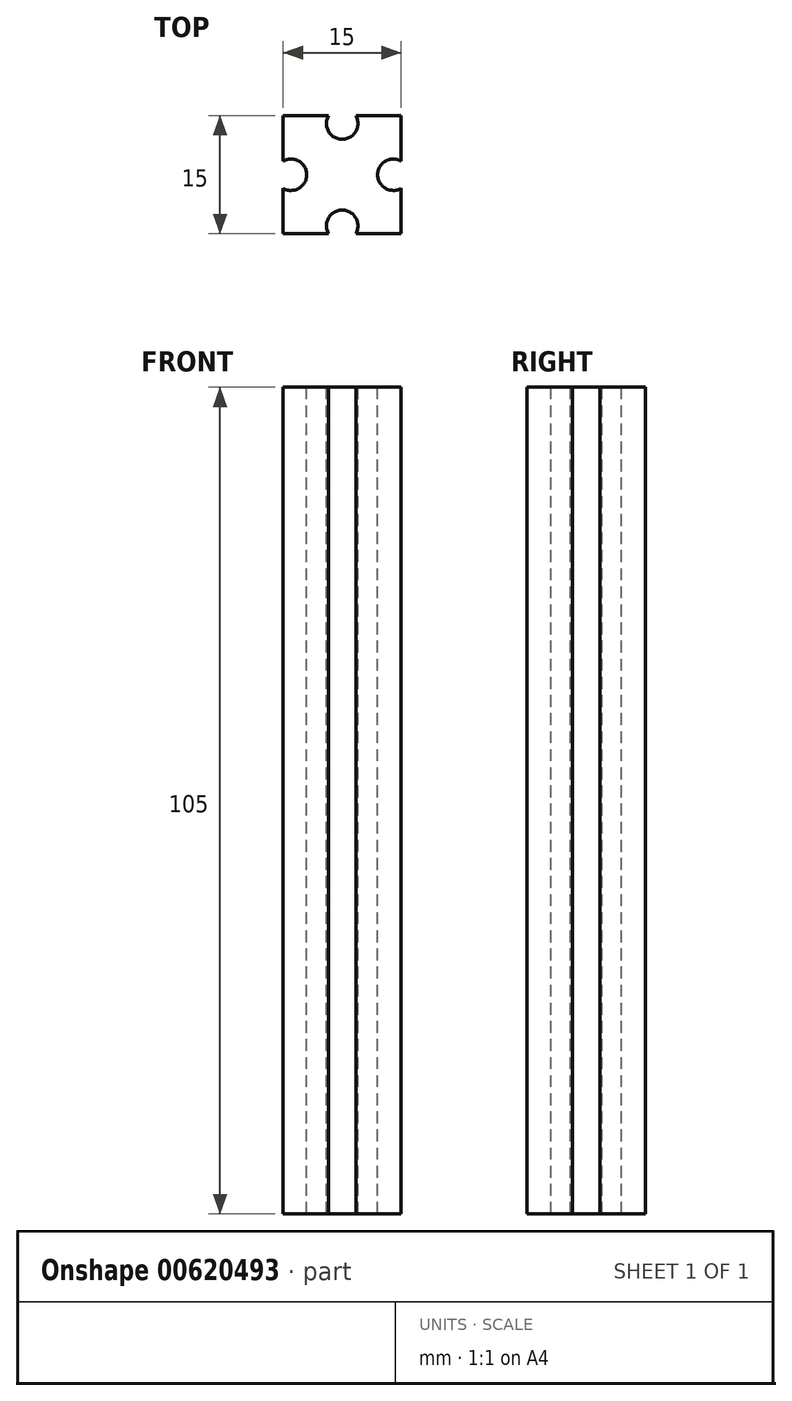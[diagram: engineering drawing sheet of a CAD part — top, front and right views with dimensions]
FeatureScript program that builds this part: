
annotation { "Feature Type Name" : "Feature", "Feature Type Description" : "" }
export const myFeature = defineFeature(function(context is Context, id is Id, definition is map)
    precondition{}
    {
        {
            var Q0;
            Q0=qCreatedBy(makeId("Top.planeOp"),FACE);
            var sketch = newSketch(context, id + "F0", { "sketchPlane" : qUnion([Q0])});
            skLineSegment(sketch, "E0.bottom", {"start": v(-11.37, 10.06) * mm, "end": v(3.63, 10.06) * mm});
            skLineSegment(sketch, "E0.top", {"start": v(-11.37, -4.94) * mm, "end": v(3.63, -4.94) * mm});
            skLineSegment(sketch, "E0.left", {"start": v(-11.37, 10.06) * mm, "end": v(-11.37, -4.94) * mm});
            skLineSegment(sketch, "E0.right", {"start": v(3.63, 10.06) * mm, "end": v(3.63, -4.94) * mm});
            skSolve(sketch);
        }
        {
            var Q0;
            Q0=makeQuery(id+"F0.imprint","IMPRINT",FACE,{"disambiguationData":[TD([[makeQuery(id+"F0.imprint","IMPRINT",EDGE,{"derivedFrom":sQuery(id+"F0.wireOp",EDGE,"E0.bottom")}),-1.0]])]});
            extrude(context, id + "F1", {"entities" : qUnion([Q0]), "depth" : 105 * mm, "offsetDistance" : 25.4 * mm});
        }
        {
            var Q0;
            Q0=makeQuery(id+"F1.opExtrude","CAP_FACE",FACE,{"disambiguationData":[OSD([sQuery(id+"F0.wireOp",EDGE,"E0.bottom"),sQuery(id+"F0.wireOp",EDGE,"E0.top"),sQuery(id+"F0.wireOp",EDGE,"E0.left"),sQuery(id+"F0.wireOp",EDGE,"E0.right")])],"isStart":false});
            var sketch = newSketch(context, id + "F2", { "sketchPlane" : qUnion([Q0])});
            skCircle(sketch, "E1", {"center": v(-10.37, 2.56) * mm, "radius": 2 * mm});
            skPoint(sketch, "E1.centerSnap0", {"position": v(-11.37, 2.56) * mm});
            skSolve(sketch);
        }
        {
            var Q0;
            {var subQ0=sQuery(id+"F2.wireOp",EDGE,"E1");var subQ1=makeQuery(id+"F1.opExtrude","CAP_EDGE",EDGE,{"disambiguationData":[OSD([sQuery(id+"F0.wireOp",EDGE,"E0.left")])],"isStart":false});var subQ2=makeQuery(id+"F2.imprint","INTERSECT",VERTEX,{"disambiguationData":[OD(0.0)],"derivedFrom":[subQ1,subQ0]});Q0=makeQuery(id+"F2.imprint","IMPRINT",FACE,{"disambiguationData":[TD([[makeQuery(id+"F2.imprint","IMPRINT",EDGE,{"disambiguationData":[TD([[subQ2,1.0]])],"derivedFrom":subQ0}),1.0]])]});}
            extrude(context, id + "F3", {"entities" : qUnion([Q0]), "operationType" : NewBodyOperationType.REMOVE, "oppositeDirection" : true, "depth" : 105 * mm, "offsetDistance" : 25.4 * mm});
        }
        {
            var Q0;
            Q0=makeQuery(id+"F1.opExtrude","CAP_FACE",FACE,{"disambiguationData":[OSD([sQuery(id+"F0.wireOp",EDGE,"E0.bottom"),sQuery(id+"F0.wireOp",EDGE,"E0.top"),sQuery(id+"F0.wireOp",EDGE,"E0.left"),sQuery(id+"F0.wireOp",EDGE,"E0.right")])],"isStart":false});
            var sketch = newSketch(context, id + "F4", { "sketchPlane" : qUnion([Q0])});
            skCircle(sketch, "E2", {"center": v(-3.87, 9.06) * mm, "radius": 2 * mm});
            skPoint(sketch, "E2.centerSnap0", {"position": v(-3.87, 10.06) * mm});
            skSolve(sketch);
        }
        {
            var Q0;
            {var subQ0=sQuery(id+"F4.wireOp",EDGE,"E2");var subQ1=makeQuery(id+"F1.opExtrude","CAP_EDGE",EDGE,{"disambiguationData":[OSD([sQuery(id+"F0.wireOp",EDGE,"E0.bottom")])],"isStart":false});var subQ2=makeQuery(id+"F4.imprint","INTERSECT",VERTEX,{"disambiguationData":[OD(0.0)],"derivedFrom":[subQ1,subQ0]});Q0=makeQuery(id+"F4.imprint","IMPRINT",FACE,{"disambiguationData":[TD([[makeQuery(id+"F4.imprint","IMPRINT",EDGE,{"disambiguationData":[TD([[subQ2,-1.0]])],"derivedFrom":subQ0}),1.0]])]});}
            extrude(context, id + "F5", {"entities" : qUnion([Q0]), "operationType" : NewBodyOperationType.REMOVE, "oppositeDirection" : true, "depth" : 105 * mm, "offsetDistance" : 25.4 * mm});
        }
        {
            var Q0;
            Q0=makeQuery(id+"F1.opExtrude","CAP_FACE",FACE,{"disambiguationData":[OSD([sQuery(id+"F0.wireOp",EDGE,"E0.bottom"),sQuery(id+"F0.wireOp",EDGE,"E0.top"),sQuery(id+"F0.wireOp",EDGE,"E0.left"),sQuery(id+"F0.wireOp",EDGE,"E0.right")])],"isStart":false});
            var sketch = newSketch(context, id + "F6", { "sketchPlane" : qUnion([Q0])});
            skCircle(sketch, "E3", {"center": v(2.63, 2.56) * mm, "radius": 2 * mm});
            skPoint(sketch, "E3.centerSnap0", {"position": v(3.63, 2.56) * mm});
            skCircle(sketch, "E4", {"center": v(-3.87, -3.94) * mm, "radius": 2 * mm});
            skPoint(sketch, "E4.centerSnap0", {"position": v(-3.87, -4.94) * mm});
            skSolve(sketch);
        }
        {
            var Q0;
            {var subQ0=sQuery(id+"F6.wireOp",EDGE,"E4");var subQ1=makeQuery(id+"F1.opExtrude","CAP_EDGE",EDGE,{"disambiguationData":[OSD([sQuery(id+"F0.wireOp",EDGE,"E0.top")])],"isStart":false});var subQ2=makeQuery(id+"F6.imprint","INTERSECT",VERTEX,{"disambiguationData":[OD(0.0)],"derivedFrom":[subQ1,subQ0]});Q0=makeQuery(id+"F6.imprint","IMPRINT",FACE,{"disambiguationData":[TD([[makeQuery(id+"F6.imprint","IMPRINT",EDGE,{"disambiguationData":[TD([[subQ2,1.0]])],"derivedFrom":subQ0}),1.0]])]});}
            var Q1;
            {var subQ0=sQuery(id+"F6.wireOp",EDGE,"E3");var subQ1=makeQuery(id+"F1.opExtrude","CAP_EDGE",EDGE,{"disambiguationData":[OSD([sQuery(id+"F0.wireOp",EDGE,"E0.right")])],"isStart":false});var subQ2=makeQuery(id+"F6.imprint","INTERSECT",VERTEX,{"disambiguationData":[OD(0.0)],"derivedFrom":[subQ1,subQ0]});Q1=makeQuery(id+"F6.imprint","IMPRINT",FACE,{"disambiguationData":[TD([[makeQuery(id+"F6.imprint","IMPRINT",EDGE,{"disambiguationData":[TD([[subQ2,-1.0]])],"derivedFrom":subQ0}),1.0]])]});}
            extrude(context, id + "F7", {"entities" : qUnion([Q0, Q1]), "operationType" : NewBodyOperationType.REMOVE, "oppositeDirection" : true, "depth" : 105 * mm, "offsetDistance" : 25.4 * mm});
        }
    });
